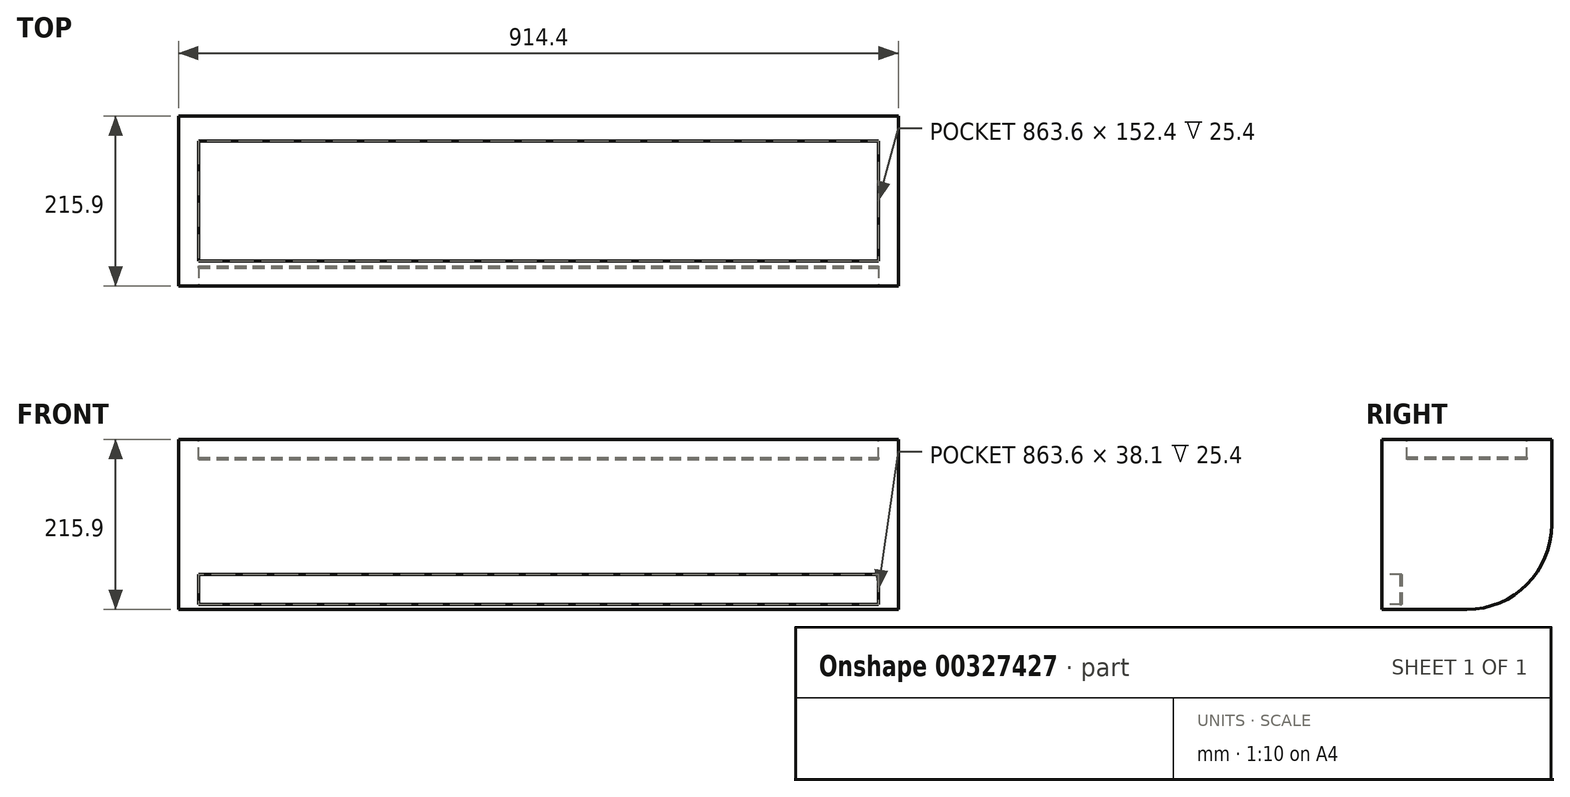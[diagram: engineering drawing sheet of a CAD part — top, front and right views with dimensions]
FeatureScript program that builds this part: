
annotation { "Feature Type Name" : "Feature", "Feature Type Description" : "" }
export const myFeature = defineFeature(function(context is Context, id is Id, definition is map)
    precondition{}
    {
        {
            var Q0;
            Q0=qCreatedBy(makeId("Right.planeOp"),FACE);
            var sketch = newSketch(context, id + "F0", { "sketchPlane" : qUnion([Q0])});
            skLineSegment(sketch, "E0.bottom", {"start": v(-107.95, 0) * mm, "end": v(-215.9, 0) * mm});
            skLineSegment(sketch, "E0.top", {"start": v(0, 215.9) * mm, "end": v(-215.9, 215.9) * mm});
            skLineSegment(sketch, "E0.left", {"start": v(0, 107.95) * mm, "end": v(0, 215.9) * mm});
            skLineSegment(sketch, "E0.right", {"start": v(-215.9, 0) * mm, "end": v(-215.9, 215.9) * mm});
            skPoint(sketch, "E1.visualSharp", {"position": v(0, 0) * mm});
            skArc(sketch, "E1.filletArc", {"start": v(-107.95, 0) * mm, "mid": v(-31.62, 31.62) * mm, "end": v(0, 107.95) * mm});
            skLineSegment(sketch, "E2", {"start": v(-107.95, 107.95) * mm, "end": v(-107.95, 215.9) * mm, "construction": true});
            skSolve(sketch);
        }
        {
            var Q0;
            Q0 = qSketchRegion(id + "F0", true);
            extrude(context, id + "F1", {"entities" : qUnion([Q0]), "depth" : 914.4 * mm, "symmetric" : true});
        }
        {
            var Q0;
            Q0=makeQuery(id+"F1.opExtrude","SWEPT_FACE",FACE,{"disambiguationData":[OSD([sQuery(id+"F0.wireOp",EDGE,"E0.right")])]});
            var sketch = newSketch(context, id + "F2", { "sketchPlane" : qUnion([Q0])});
            skLineSegment(sketch, "E3.bottom", {"start": v(-431.8, 44.45) * mm, "end": v(431.8, 44.45) * mm});
            skLineSegment(sketch, "E3.top", {"start": v(-431.8, 6.35) * mm, "end": v(431.8, 6.35) * mm});
            skLineSegment(sketch, "E3.left", {"start": v(-431.8, 44.45) * mm, "end": v(-431.8, 6.35) * mm});
            skLineSegment(sketch, "E3.right", {"start": v(431.8, 44.45) * mm, "end": v(431.8, 6.35) * mm});
            skPoint(sketch, "E4", {"position": v(0, 44.45) * mm});
            skSolve(sketch);
        }
        {
            var Q0;
            Q0 = qSketchRegion(id + "F2", true);
            extrude(context, id + "F3", {"entities" : qUnion([Q0]), "operationType" : NewBodyOperationType.REMOVE, "oppositeDirection" : true, "depth" : 25.4 * mm});
        }
        {
            var Q0;
            Q0=makeQuery(id+"F1.opExtrude","SWEPT_FACE",FACE,{"disambiguationData":[OSD([sQuery(id+"F0.wireOp",EDGE,"E0.top")])]});
            var sketch = newSketch(context, id + "F4", { "sketchPlane" : qUnion([Q0])});
            skLineSegment(sketch, "E5.bottom", {"start": v(-431.8, -31.75) * mm, "end": v(431.8, -31.75) * mm});
            skLineSegment(sketch, "E5.top", {"start": v(-431.8, -184.15) * mm, "end": v(431.8, -184.15) * mm});
            skLineSegment(sketch, "E5.left", {"start": v(-431.8, -31.75) * mm, "end": v(-431.8, -184.15) * mm});
            skLineSegment(sketch, "E5.right", {"start": v(431.8, -31.75) * mm, "end": v(431.8, -184.15) * mm});
            skPoint(sketch, "E6", {"position": v(0, -31.75) * mm});
            skPoint(sketch, "E7", {"position": v(431.8, -107.95) * mm});
            skLineSegment(sketch, "E8", {"start": v(431.8, -107.95) * mm, "end": v(457.2, -107.95) * mm, "construction": true});
            skSolve(sketch);
        }
        {
            var Q0;
            Q0 = qSketchRegion(id + "F4", true);
            extrude(context, id + "F5", {"entities" : qUnion([Q0]), "operationType" : NewBodyOperationType.REMOVE, "oppositeDirection" : true, "depth" : 25.4 * mm});
        }
        {
            var Q0;
            Q0=makeQuery(id+"F5.boolean.opBoolean","COPY",FACE,{"derivedFrom":makeQuery(id+"F5.opExtrude","CAP_FACE",FACE,{"disambiguationData":[OSD([sQuery(id+"F4.wireOp",EDGE,"E5.bottom"),sQuery(id+"F4.wireOp",EDGE,"E5.top"),sQuery(id+"F4.wireOp",EDGE,"E5.left"),sQuery(id+"F4.wireOp",EDGE,"E5.right")])],"isStart":false})});
            extrude(context, id + "F6", {"entities" : qUnion([Q0]), "depth" : 2.54 * mm});
        }
        {
            var Q0;
            Q0=makeQuery(id+"F3.boolean.opBoolean","COPY",FACE,{"derivedFrom":makeQuery(id+"F3.opExtrude","CAP_FACE",FACE,{"disambiguationData":[OSD([sQuery(id+"F2.wireOp",EDGE,"E3.bottom"),sQuery(id+"F2.wireOp",EDGE,"E3.top"),sQuery(id+"F2.wireOp",EDGE,"E3.left"),sQuery(id+"F2.wireOp",EDGE,"E3.right")])],"isStart":false})});
            extrude(context, id + "F7", {"entities" : qUnion([Q0]), "depth" : 2.54 * mm});
        }
    });
